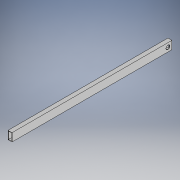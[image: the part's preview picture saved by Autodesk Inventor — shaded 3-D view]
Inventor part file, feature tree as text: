
AUTODESK INVENTOR PART (.ipt)
format: ipt  version: 2018 (Build 220112000, 112)  size: 108,032 bytes
history: native  units: in
note: dims shown in document units (in); Inventor stores cm internally (conversion verified against a paired STEP export)
features: extrude x2, sketch x2
ambient origin geometry x8: Origin, YZ Plane, XZ Plane, XY Plane, X Axis, Y Axis, Z Axis, Center Point
bodies: Solid1 (feature_tree)
feature tree (4):
  extrude  "Extrusion1"  Depth=2.0in
  extrude  "Extrusion2"  Depth=39.7in TaperAngle=0.0deg
  sketch  "Sketch1"  dims[d0=1.0in d1=2.0in]
  sketch  "Sketch2"  dims[d2=0.125in d3=39.7in d4=0.0in d5=1.0in d7=10.0in d8=0.0in d9=1.0in]
